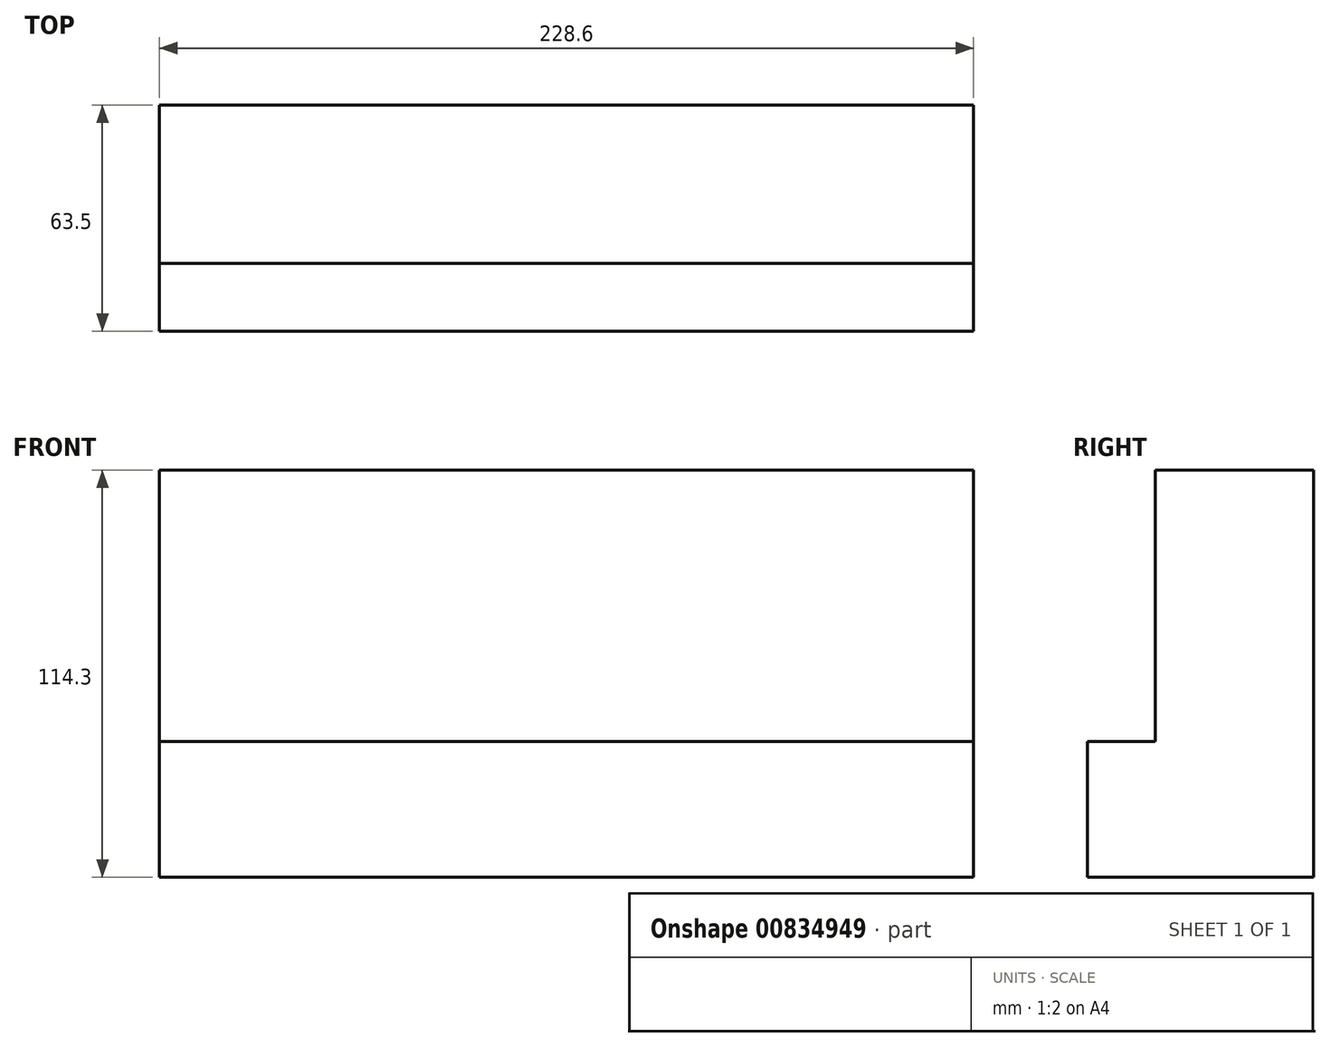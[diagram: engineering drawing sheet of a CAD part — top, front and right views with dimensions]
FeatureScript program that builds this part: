
annotation { "Feature Type Name" : "Feature", "Feature Type Description" : "" }
export const myFeature = defineFeature(function(context is Context, id is Id, definition is map)
    precondition{}
    {
        {
            var Q0;
            Q0=qCreatedBy(makeId("Top.planeOp"),FACE);
            var sketch = newSketch(context, id + "F0", { "sketchPlane" : qUnion([Q0])});
            skLineSegment(sketch, "E0.bottom", {"start": v(0, 0) * mm, "end": v(228.6, 0) * mm});
            skLineSegment(sketch, "E0.top", {"start": v(0, 63.5) * mm, "end": v(228.6, 63.5) * mm});
            skLineSegment(sketch, "E0.left", {"start": v(0, 0) * mm, "end": v(0, 63.5) * mm});
            skLineSegment(sketch, "E0.right", {"start": v(228.6, 0) * mm, "end": v(228.6, 63.5) * mm});
            skSolve(sketch);
        }
        {
            var Q0;
            Q0=qSketchRegion(id+"F0",true);
            extrude(context, id + "F1", {"entities" : qUnion([Q0]), "depth" : 114.3 * mm, "offsetDistance" : 25.4 * mm});
        }
        {
            var Q0;
            Q0=makeQuery(id+"F1.opExtrude","SWEPT_FACE",FACE,{"disambiguationData":[OSD([sQuery(id+"F0.wireOp",EDGE,"E0.right")])]});
            var sketch = newSketch(context, id + "F2", { "sketchPlane" : qUnion([Q0])});
            skLineSegment(sketch, "E1.bottom", {"start": v(0, 114.3) * mm, "end": v(19.05, 114.3) * mm});
            skLineSegment(sketch, "E1.top", {"start": v(0, 38.1) * mm, "end": v(19.05, 38.1) * mm});
            skLineSegment(sketch, "E1.left", {"start": v(0, 114.3) * mm, "end": v(0, 38.1) * mm});
            skLineSegment(sketch, "E1.right", {"start": v(19.05, 114.3) * mm, "end": v(19.05, 38.1) * mm});
            skSolve(sketch);
        }
        {
            var Q0;
            Q0 = qSketchRegion(id + "F2", true);
            extrude(context, id + "F3", {"entities" : qUnion([Q0]), "operationType" : NewBodyOperationType.REMOVE, "endBound" : BoundingType.THROUGH_ALL, "oppositeDirection" : true, "depth" : 25.4 * mm, "offsetDistance" : 25.4 * mm});
        }
    });
